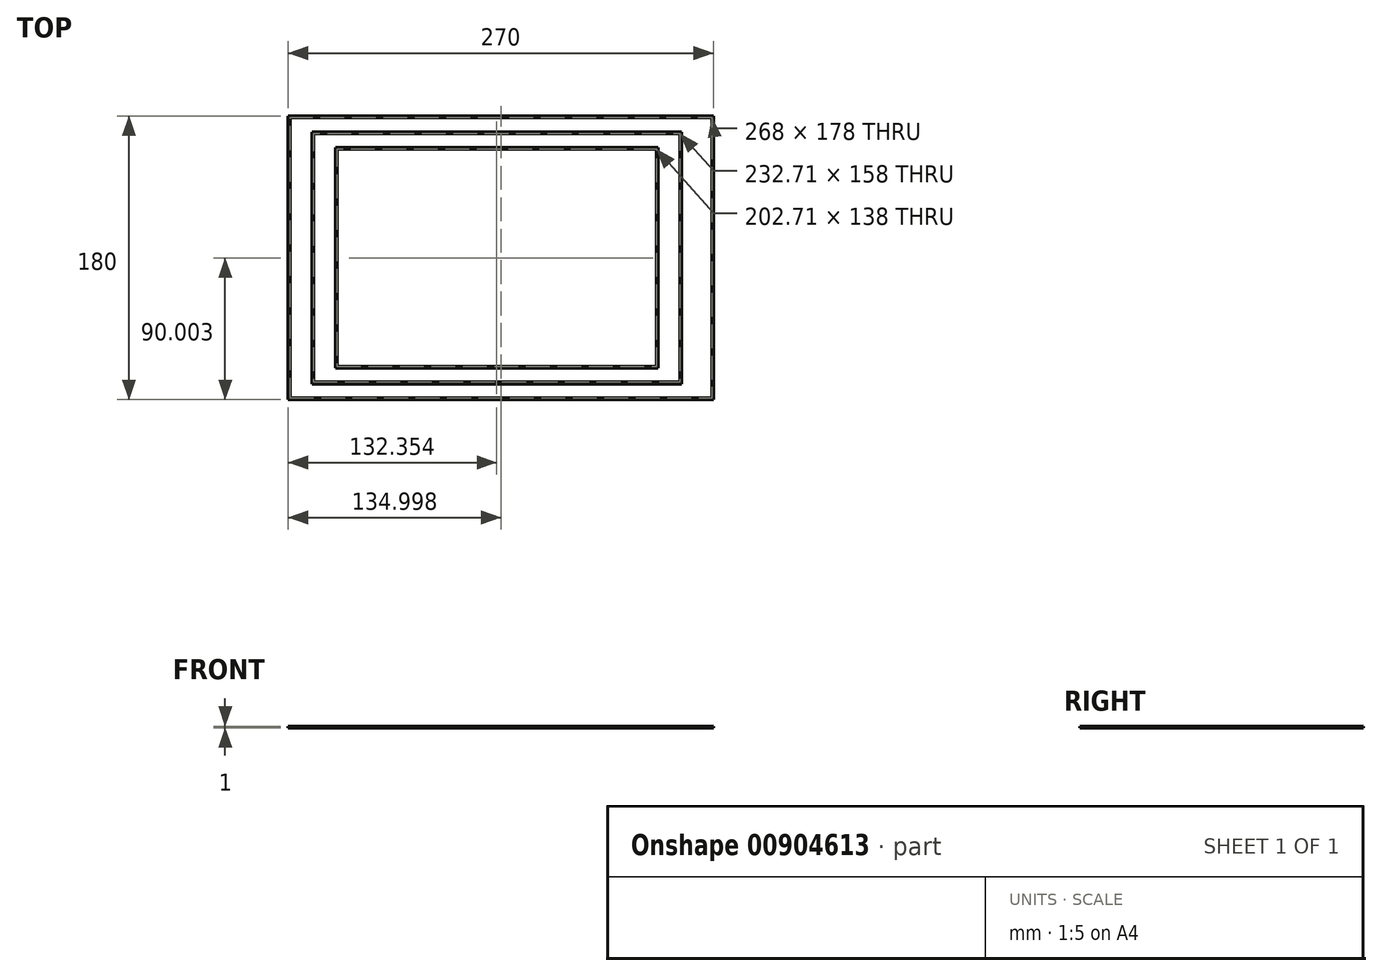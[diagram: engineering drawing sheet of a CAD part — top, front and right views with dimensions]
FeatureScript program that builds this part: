
annotation { "Feature Type Name" : "Feature", "Feature Type Description" : "" }
export const myFeature = defineFeature(function(context is Context, id is Id, definition is map)
    precondition{}
    {
        {
            assignVariable(context, id + "F0", {"name" : "LineHeight", "anyValue" : 1});
        }
        {
            var Q0;
            Q0=qCreatedBy(makeId("Top.planeOp"),FACE);
            var sketch = newSketch(context, id + "F1", { "sketchPlane" : qUnion([Q0])});
            skLineSegment(sketch, "E0.bottom", {"start": v(-91.48, 107.86) * mm, "end": v(178.52, 107.86) * mm});
            skLineSegment(sketch, "E0.top", {"start": v(-91.48, -72.14) * mm, "end": v(178.52, -72.14) * mm});
            skLineSegment(sketch, "E0.left", {"start": v(-91.48, 107.86) * mm, "end": v(-91.48, -72.14) * mm});
            skLineSegment(sketch, "E0.right", {"start": v(178.52, 107.86) * mm, "end": v(178.52, -72.14) * mm});
            skLineSegment(sketch, "E1.bottom", {"start": v(-76.48, 97.86) * mm, "end": v(158.23, 97.86) * mm});
            skLineSegment(sketch, "E1.top", {"start": v(-76.48, -62.14) * mm, "end": v(158.23, -62.14) * mm});
            skLineSegment(sketch, "E1.left", {"start": v(-76.48, 97.86) * mm, "end": v(-76.48, -62.14) * mm});
            skLineSegment(sketch, "E1.right", {"start": v(158.23, 97.86) * mm, "end": v(158.23, -62.14) * mm});
            skLineSegment(sketch, "E2.bottom", {"start": v(-61.48, 87.86) * mm, "end": v(143.23, 87.86) * mm});
            skLineSegment(sketch, "E2.top", {"start": v(-61.48, -52.14) * mm, "end": v(143.23, -52.14) * mm});
            skLineSegment(sketch, "E2.left", {"start": v(-61.48, 87.86) * mm, "end": v(-61.48, -52.14) * mm});
            skLineSegment(sketch, "E2.right", {"start": v(143.23, 87.86) * mm, "end": v(143.23, -52.14) * mm});
            skLineSegment(sketch, "E3", {"start": v(-90.48, 106.86) * mm, "end": v(177.52, 106.86) * mm});
            skLineSegment(sketch, "E4", {"start": v(177.52, 106.86) * mm, "end": v(177.52, -71.14) * mm});
            skLineSegment(sketch, "E5", {"start": v(177.52, -71.14) * mm, "end": v(-90.48, -71.14) * mm});
            skLineSegment(sketch, "E6", {"start": v(-90.48, -71.14) * mm, "end": v(-90.48, 106.86) * mm});
            skLineSegment(sketch, "E7", {"start": v(-75.48, 96.86) * mm, "end": v(157.23, 96.86) * mm});
            skLineSegment(sketch, "E8", {"start": v(157.23, 96.86) * mm, "end": v(157.23, -61.14) * mm});
            skLineSegment(sketch, "E9", {"start": v(157.23, -61.14) * mm, "end": v(-75.48, -61.14) * mm});
            skLineSegment(sketch, "E10", {"start": v(-75.48, -61.14) * mm, "end": v(-75.48, 96.86) * mm});
            skLineSegment(sketch, "E11", {"start": v(-60.48, 86.86) * mm, "end": v(142.23, 86.86) * mm});
            skLineSegment(sketch, "E12", {"start": v(142.23, 86.86) * mm, "end": v(142.23, -51.14) * mm});
            skLineSegment(sketch, "E13", {"start": v(142.23, -51.14) * mm, "end": v(-60.48, -51.14) * mm});
            skLineSegment(sketch, "E14", {"start": v(-60.48, -51.14) * mm, "end": v(-60.48, 86.86) * mm});
            skSolve(sketch);
        }
        {
            var Q0;
            Q0=makeQuery(id+"F1.imprint","IMPRINT",FACE,{"disambiguationData":[TD([[makeQuery(id+"F1.imprint","IMPRINT",EDGE,{"derivedFrom":sQuery(id+"F1.wireOp",EDGE,"E0.bottom")}),-1.0]])]});
            var Q1;
            Q1=makeQuery(id+"F1.imprint","IMPRINT",FACE,{"disambiguationData":[TD([[makeQuery(id+"F1.imprint","IMPRINT",EDGE,{"derivedFrom":sQuery(id+"F1.wireOp",EDGE,"E1.bottom")}),-1.0]])]});
            var Q2;
            Q2=makeQuery(id+"F1.imprint","IMPRINT",FACE,{"disambiguationData":[TD([[makeQuery(id+"F1.imprint","IMPRINT",EDGE,{"derivedFrom":sQuery(id+"F1.wireOp",EDGE,"E2.bottom")}),-1.0]])]});
            var Q3;
            Q3=makeQuery(id+"F1.imprint","IMPRINT",FACE,{"disambiguationData":[TD([[makeQuery(id+"F1.imprint","IMPRINT",EDGE,{"derivedFrom":sQuery(id+"F1.wireOp",EDGE,"iO6pfZbY-7ntN-yKzr-tIri-R5R3f5lDf0fY")}),1.0]])]});
            var Q4;
            Q4=makeQuery(id+"F1.imprint","IMPRINT",FACE,{"disambiguationData":[TD([[makeQuery(id+"F1.imprint","IMPRINT",EDGE,{"derivedFrom":sQuery(id+"F1.wireOp",EDGE,"f7fcbfd7-52aa-416a-90d2-34237ff1b969.bottom")}),-1.0]])]});
            var Q5;
            Q5=makeQuery(id+"F1.imprint","IMPRINT",FACE,{"disambiguationData":[TD([[makeQuery(id+"F1.imprint","IMPRINT",EDGE,{"derivedFrom":sQuery(id+"F1.wireOp",EDGE,"HmofG7po-VB2C-NLRk-urQ5-j8slKDY0yj7J")}),1.0]])]});
            extrude(context, id + "F2", {"entities" : qUnion([Q0, Q1, Q2, Q3, Q4, Q5]), "depth" : (getVariable(context, 'LineHeight')) * mm, "offsetDistance" : 25 * mm});
        }
    });
